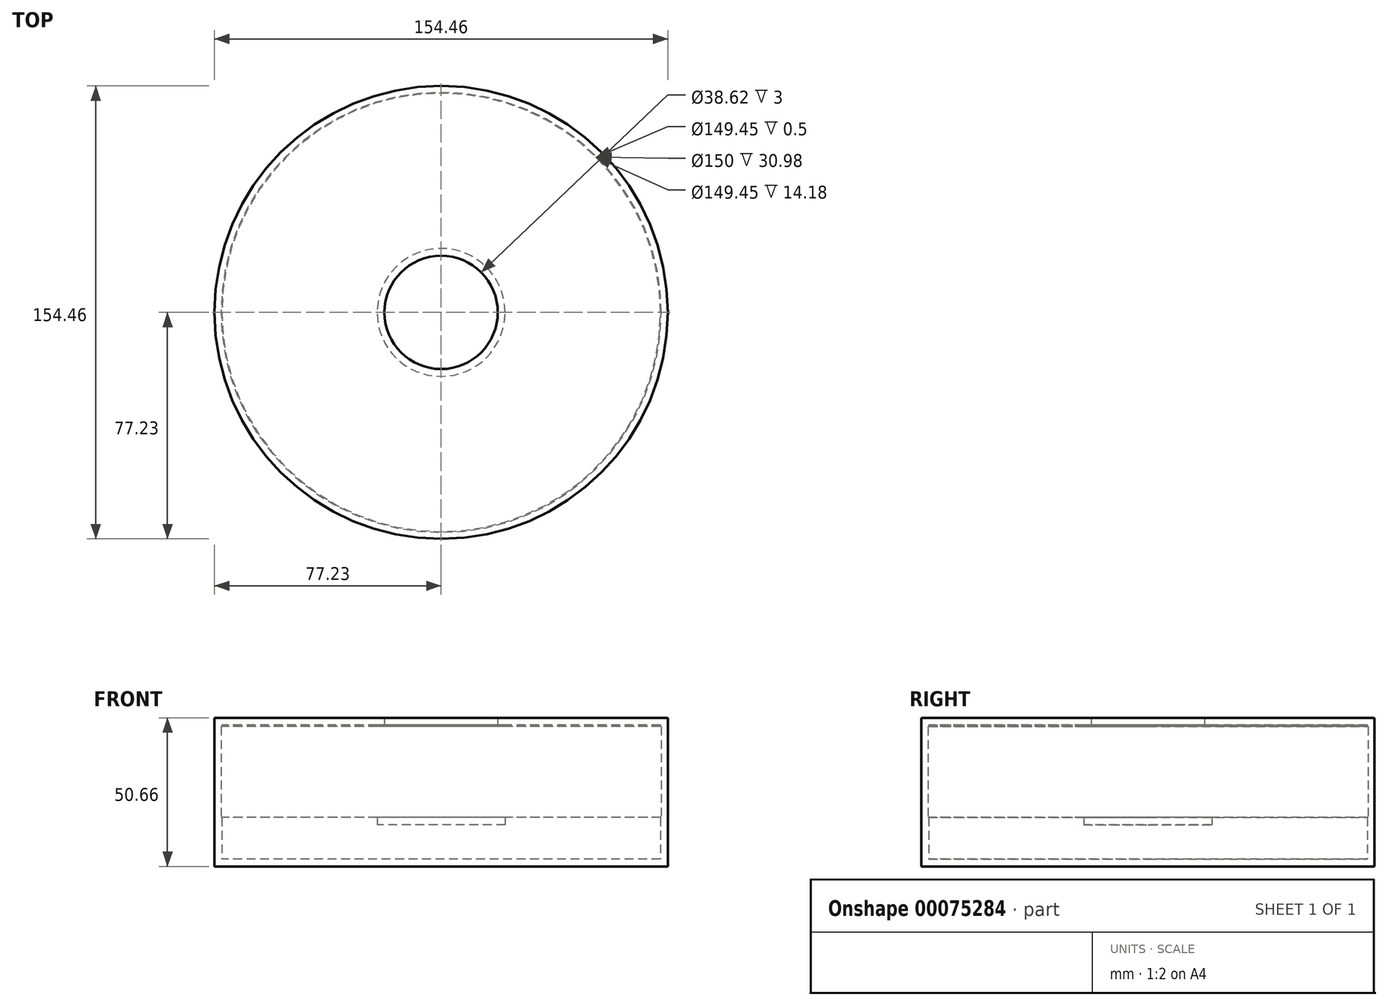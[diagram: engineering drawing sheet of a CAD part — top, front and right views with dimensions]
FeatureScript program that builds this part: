
annotation { "Feature Type Name" : "Feature", "Feature Type Description" : "" }
export const myFeature = defineFeature(function(context is Context, id is Id, definition is map)
    precondition{}
    {
        {
            var Q0;
            Q0=qCreatedBy(makeId("Top.planeOp"),FACE);
            var sketch = newSketch(context, id + "F0", { "sketchPlane" : qUnion([Q0])});
            skCircle(sketch, "E0", {"center": v(0, 0) * mm, "radius": 77.23 * mm});
            skCircle(sketch, "E1", {"center": v(0, 0) * mm, "radius": 19.31 * mm});
            skSolve(sketch);
        }
        {
            var Q0;
            Q0=makeQuery(id+"F0.imprint","IMPRINT",FACE,{"disambiguationData":[TD([[makeQuery(id+"F0.imprint","IMPRINT",EDGE,{"derivedFrom":sQuery(id+"F0.wireOp",EDGE,"E1")}),1.0]])]});
            extrude(context, id + "F1", {"entities" : qUnion([Q0]), "depth" : 16.68 * mm});
        }
        {
            var Q0;
            Q0 = qSketchRegion(id + "F0", true);
            extrude(context, id + "F2", {"entities" : qUnion([Q0]), "operationType" : NewBodyOperationType.ADD, "depth" : 50.66 * mm});
        }
        {
            var Q0;
            Q0=makeQuery(id+"F2.opExtrude","SWEPT_FACE",FACE,{"disambiguationData":[OSD([sQuery(id+"F0.wireOp",EDGE,"E1")])]});
            var Q1;
            Q1=makeQuery(id+"F1.opExtrude","SWEPT_BODY",BODY,{"disambiguationData":[OSD([sQuery(id+"F0.wireOp",EDGE,"E1")])]});
            shell(context, id + "F3", {"isHollow" : true, "entities" : qUnion([Q0]), "parts" : qUnion([Q1]), "thickness" : 2.5 * mm});
        }
        {
            var Q0;
            Q0=makeQuery(id+"F1.opExtrude","CAP_FACE",FACE,{"disambiguationData":[OSD([sQuery(id+"F0.wireOp",EDGE,"E1")])],"isStart":false});
            var sketch = newSketch(context, id + "F4", { "sketchPlane" : qUnion([Q0])});
            skCircle(sketch, "E2", {"center": v(0, 0) * mm, "radius": 75 * mm});
            skSolve(sketch);
        }
        {
            var Q0;
            Q0 = qSketchRegion(id + "F4", true);
            extrude(context, id + "F5", {"entities" : qUnion([Q0]), "operationType" : NewBodyOperationType.REMOVE, "depth" : 30.98 * mm});
        }
    });
